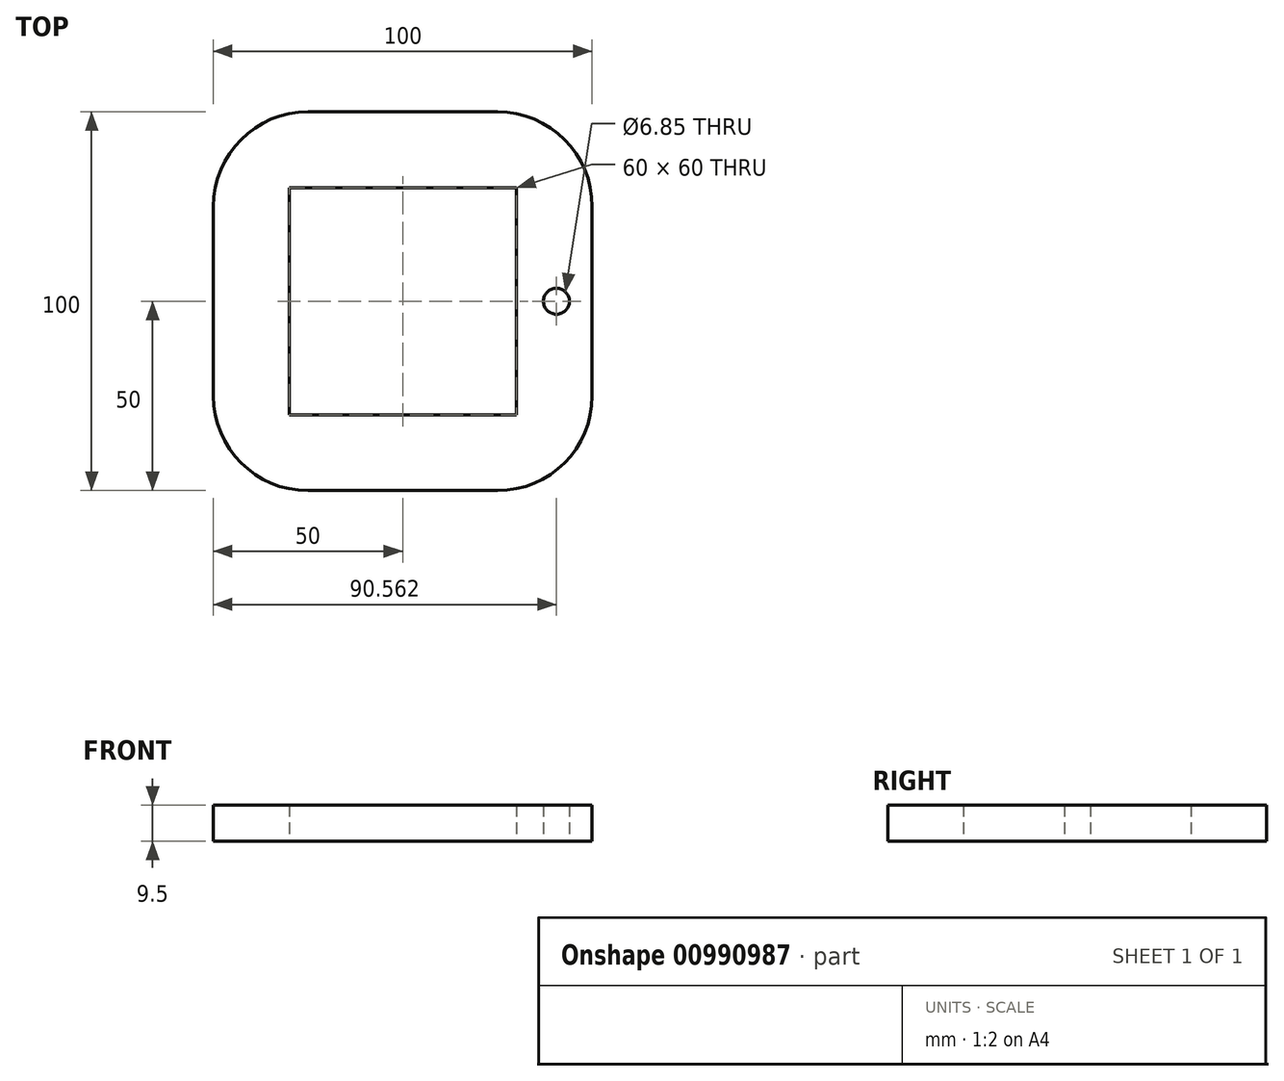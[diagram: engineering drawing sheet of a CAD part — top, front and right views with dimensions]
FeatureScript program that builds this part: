
annotation { "Feature Type Name" : "Feature", "Feature Type Description" : "" }
export const myFeature = defineFeature(function(context is Context, id is Id, definition is map)
    precondition{}
    {
        {
            var Q0;
            Q0=qCreatedBy(makeId("Top.planeOp"),FACE);
            var sketch = newSketch(context, id + "F0", { "sketchPlane" : qUnion([Q0])});
            skLineSegment(sketch, "E0.bottom", {"start": v(30, -30) * mm, "end": v(-30, -30) * mm});
            skLineSegment(sketch, "E0.top", {"start": v(30, 30) * mm, "end": v(-30, 30) * mm});
            skLineSegment(sketch, "E0.left", {"start": v(30, -30) * mm, "end": v(30, 30) * mm});
            skLineSegment(sketch, "E0.right", {"start": v(-30, -30) * mm, "end": v(-30, 30) * mm});
            skPoint(sketch, "E0.middle", {"position": v(0, 0) * mm});
            skLineSegment(sketch, "E1.bottom", {"start": v(25, -50) * mm, "end": v(-25, -50) * mm});
            skLineSegment(sketch, "E1.top", {"start": v(25, 50) * mm, "end": v(-25, 50) * mm});
            skLineSegment(sketch, "E1.left", {"start": v(50, -25) * mm, "end": v(50, 25) * mm});
            skLineSegment(sketch, "E1.right", {"start": v(-50, -25) * mm, "end": v(-50, 25) * mm});
            skPoint(sketch, "E2.visualSharp", {"position": v(-50, 50) * mm});
            skArc(sketch, "E2.filletArc", {"start": v(-25, 50) * mm, "mid": v(-42.68, 42.68) * mm, "end": v(-50, 25) * mm});
            skPoint(sketch, "E3.visualSharp", {"position": v(-50, -50) * mm});
            skArc(sketch, "E3.filletArc", {"start": v(-50, -25) * mm, "mid": v(-42.68, -42.68) * mm, "end": v(-25, -50) * mm});
            skPoint(sketch, "E4.visualSharp", {"position": v(50, -50) * mm});
            skArc(sketch, "E4.filletArc", {"start": v(25, -50) * mm, "mid": v(42.68, -42.68) * mm, "end": v(50, -25) * mm});
            skPoint(sketch, "E5.visualSharp", {"position": v(50, 50) * mm});
            skArc(sketch, "E5.filletArc", {"start": v(50, 25) * mm, "mid": v(42.68, 42.68) * mm, "end": v(25, 50) * mm});
            skCircle(sketch, "E6", {"center": v(-40.56, 0) * mm, "radius": 3.43 * mm});
            skLineSegment(sketch, "E7", {"start": v(0, 50) * mm, "end": v(0, -50) * mm, "construction": true});
            skCircle(sketch, "E8.MirrorC", {"center": v(40.56, 0) * mm, "radius": 3.43 * mm});
            skSolve(sketch);
        }
        {
            var Q0;
            Q0=makeQuery(id+"F0.imprint","IMPRINT",FACE,{"disambiguationData":[TD([[makeQuery(id+"F0.imprint","IMPRINT",EDGE,{"derivedFrom":sQuery(id+"F0.wireOp",EDGE,"E0.bottom")}),1.0]])]});
            extrude(context, id + "F1", {"entities" : qUnion([Q0]), "depth" : 5 * mm, "offsetDistance" : 25 * mm});
        }
        {
            var Q0;
            Q0=makeQuery(id+"F0.imprint","IMPRINT",FACE,{"disambiguationData":[TD([[makeQuery(id+"F0.imprint","IMPRINT",EDGE,{"derivedFrom":sQuery(id+"F0.wireOp",EDGE,"E6")}),1.0]])]});
            var Q1;
            Q1=makeQuery(id+"F0.imprint","IMPRINT",FACE,{"disambiguationData":[TD([[makeQuery(id+"F0.imprint","IMPRINT",EDGE,{"derivedFrom":sQuery(id+"F0.wireOp",EDGE,"E8.MirrorC")}),-1.0]])]});
            extrude(context, id + "F2", {"entities" : qUnion([Q0, Q1]), "operationType" : NewBodyOperationType.ADD, "depth" : 9.5 * mm, "offsetDistance" : 25 * mm});
        }
    });
